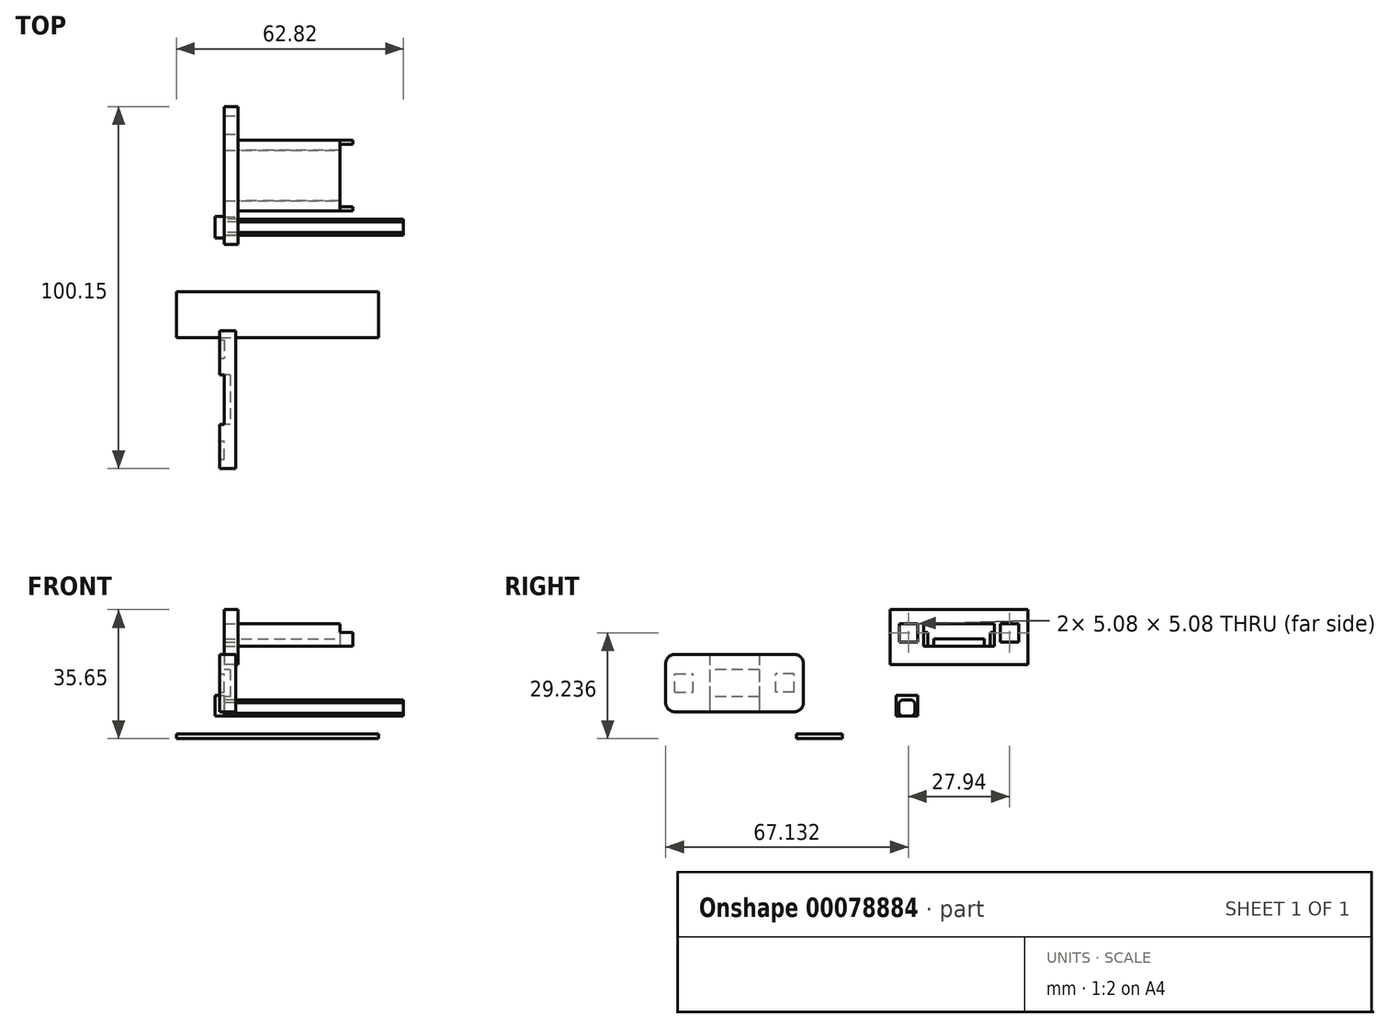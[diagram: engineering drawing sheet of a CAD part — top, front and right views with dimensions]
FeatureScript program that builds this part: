
annotation { "Feature Type Name" : "Feature", "Feature Type Description" : "" }
export const myFeature = defineFeature(function(context is Context, id is Id, definition is map)
    precondition{}
    {
        {
            var Q0;
            Q0=qCreatedBy(makeId("Front.planeOp"),FACE);
            var sketch = newSketch(context, id + "F0", { "sketchPlane" : qUnion([Q0])});
            skLineSegment(sketch, "E0.bottom", {"start": v(-13.29, 11.9) * mm, "end": v(42.6, 11.9) * mm});
            skLineSegment(sketch, "E0.top", {"start": v(-13.29, 10.63) * mm, "end": v(42.6, 10.63) * mm});
            skLineSegment(sketch, "E0.left", {"start": v(-13.29, 11.9) * mm, "end": v(-13.29, 10.63) * mm});
            skLineSegment(sketch, "E0.right", {"start": v(42.6, 11.9) * mm, "end": v(42.6, 10.63) * mm});
            skLineSegment(sketch, "E1.bottom", {"start": v(42.6, 11.9) * mm, "end": v(29.9, 11.9) * mm});
            skLineSegment(sketch, "E1.top", {"start": v(42.6, 16.98) * mm, "end": v(29.9, 16.98) * mm});
            skLineSegment(sketch, "E1.left", {"start": v(42.6, 11.9) * mm, "end": v(42.6, 16.98) * mm});
            skLineSegment(sketch, "E1.right", {"start": v(29.9, 11.9) * mm, "end": v(29.9, 16.98) * mm});
            skSolve(sketch);
        }
        {
            var Q0;
            Q0=makeQuery(id+"F0.imprint","IMPRINT",FACE,{"disambiguationData":[TD([[makeQuery(id+"F0.imprint","IMPRINT",EDGE,{"derivedFrom":sQuery(id+"F0.wireOp",EDGE,"E1.bottom")}),-1.0]])]});
            var Q1;
            Q1=makeQuery(id+"F0.imprint","IMPRINT",FACE,{"disambiguationData":[TD([[makeQuery(id+"F0.imprint","IMPRINT",EDGE,{"derivedFrom":sQuery(id+"F0.wireOp",EDGE,"E0.bottom")}),-1.0]])]});
            extrude(context, id + "F1", {"entities" : qUnion([Q0, Q1]), "depth" : 12.7 * mm});
        }
        {
            var Q0;
            Q0=qCreatedBy(makeId("Right.planeOp"),FACE);
            var sketch = newSketch(context, id + "F2", { "sketchPlane" : qUnion([Q0])});
            skLineSegment(sketch, "E2.bottom", {"start": v(-46.4, 33.9) * mm, "end": v(-13.37, 33.9) * mm});
            skLineSegment(sketch, "E2.top", {"start": v(-46.4, 18.02) * mm, "end": v(-13.37, 18.02) * mm});
            skLineSegment(sketch, "E2.left", {"start": v(-48.93, 31.35) * mm, "end": v(-48.93, 20.56) * mm});
            skLineSegment(sketch, "E2.right", {"start": v(-10.83, 31.35) * mm, "end": v(-10.83, 20.56) * mm});
            skPoint(sketch, "E3.visualSharp", {"position": v(-10.83, 33.9) * mm});
            skArc(sketch, "E3.filletArc", {"start": v(-10.83, 31.35) * mm, "mid": v(-11.58, 33.15) * mm, "end": v(-13.37, 33.9) * mm});
            skPoint(sketch, "E4.visualSharp", {"position": v(-48.93, 33.9) * mm});
            skArc(sketch, "E4.filletArc", {"start": v(-46.4, 33.9) * mm, "mid": v(-48.19, 33.15) * mm, "end": v(-48.93, 31.35) * mm});
            skPoint(sketch, "E5.visualSharp", {"position": v(-48.93, 18.02) * mm});
            skArc(sketch, "E5.filletArc", {"start": v(-48.93, 20.56) * mm, "mid": v(-48.19, 18.76) * mm, "end": v(-46.4, 18.02) * mm});
            skPoint(sketch, "E6.visualSharp", {"position": v(-10.83, 18.02) * mm});
            skArc(sketch, "E6.filletArc", {"start": v(-13.37, 18.02) * mm, "mid": v(-11.58, 18.76) * mm, "end": v(-10.83, 20.56) * mm});
            skSolve(sketch);
        }
        {
            var Q0;
            Q0=makeQuery(id+"F2.imprint","IMPRINT",FACE,{"disambiguationData":[TD([[makeQuery(id+"F2.imprint","IMPRINT",EDGE,{"derivedFrom":sQuery(id+"F2.wireOp",EDGE,"E2.bottom")}),-1.0]])]});
            extrude(context, id + "F3", {"entities" : qUnion([Q0]), "depth" : 3.17 * mm});
        }
        {
            var Q0;
            Q0=makeQuery(id+"F3.opExtrude","CAP_FACE",FACE,{"disambiguationData":[OSD([sQuery(id+"F2.wireOp",EDGE,"E2.bottom"),sQuery(id+"F2.wireOp",EDGE,"E2.top"),sQuery(id+"F2.wireOp",EDGE,"E2.left"),sQuery(id+"F2.wireOp",EDGE,"E2.right")])],"isStart":true});
            var sketch = newSketch(context, id + "F4", { "sketchPlane" : qUnion([Q0])});
            skLineSegment(sketch, "E7.bottom", {"start": v(23.02, 29.7) * mm, "end": v(36.74, 29.7) * mm});
            skLineSegment(sketch, "E7.top", {"start": v(23.02, 22.2) * mm, "end": v(36.74, 22.2) * mm});
            skLineSegment(sketch, "E7.left", {"start": v(23.02, 29.7) * mm, "end": v(23.02, 22.2) * mm});
            skLineSegment(sketch, "E7.right", {"start": v(36.74, 29.7) * mm, "end": v(36.74, 22.2) * mm});
            skLineSegment(sketch, "E8", {"start": v(36.74, 29.7) * mm, "end": v(36.74, 33.9) * mm});
            skLineSegment(sketch, "E9", {"start": v(36.74, 22.2) * mm, "end": v(36.74, 18.02) * mm});
            skLineSegment(sketch, "E10", {"start": v(23.02, 22.2) * mm, "end": v(10.83, 22.2) * mm});
            skLineSegment(sketch, "E11", {"start": v(36.74, 22.2) * mm, "end": v(48.93, 22.2) * mm});
            skPoint(sketch, "E12", {"position": v(29.88, 33.9) * mm});
            skPoint(sketch, "E13", {"position": v(29.88, 18.02) * mm});
            skLineSegment(sketch, "E14", {"start": v(29.88, 33.9) * mm, "end": v(29.88, 18.02) * mm});
            skPoint(sketch, "E15", {"position": v(10.83, 25.96) * mm});
            skLineSegment(sketch, "E16.MirrorCS", {"start": v(23.02, 29.7) * mm, "end": v(23.02, 33.9) * mm});
            skLineSegment(sketch, "E17", {"start": v(23.02, 22.2) * mm, "end": v(23.02, 18.02) * mm});
            skLineSegment(sketch, "E18.bottom", {"start": v(46.4, 23.42) * mm, "end": v(41.31, 23.42) * mm});
            skLineSegment(sketch, "E18.top", {"start": v(46.4, 28.5) * mm, "end": v(41.31, 28.5) * mm});
            skLineSegment(sketch, "E18.left", {"start": v(46.4, 23.42) * mm, "end": v(46.4, 28.5) * mm});
            skLineSegment(sketch, "E18.right", {"start": v(41.31, 23.42) * mm, "end": v(41.31, 28.5) * mm});
            skPoint(sketch, "E19", {"position": v(48.93, 25.96) * mm});
            skPoint(sketch, "E20", {"position": v(46.4, 25.96) * mm});
            skPoint(sketch, "E21.MirrorP", {"position": v(13.37, 25.96) * mm});
            skLineSegment(sketch, "E22.MirrorCS", {"start": v(13.37, 28.5) * mm, "end": v(18.45, 28.5) * mm});
            skPoint(sketch, "E23.MirrorP", {"position": v(18.33, 23.42) * mm});
            skLineSegment(sketch, "E24.MirrorCS", {"start": v(13.37, 23.42) * mm, "end": v(13.37, 28.5) * mm});
            skLineSegment(sketch, "E25.MirrorCS", {"start": v(13.37, 23.42) * mm, "end": v(18.45, 23.42) * mm});
            skLineSegment(sketch, "E26.MirrorCS", {"start": v(18.45, 23.42) * mm, "end": v(18.45, 28.5) * mm});
            skLineSegment(sketch, "E27", {"start": v(46.4, 23.42) * mm, "end": v(48.93, 23.42) * mm});
            skSolve(sketch);
        }
        {
            var Q0;
            {var subQ0=sQuery(id+"F4.wireOp",EDGE,"E7.left");Q0=makeQuery(id+"F4.imprint","IMPRINT",FACE,{"disambiguationData":[TD([[makeQuery(id+"F4.imprint","IMPRINT",EDGE,{"derivedFrom":subQ0}),1.0]])]});}
            var Q1;
            {var subQ0=sQuery(id+"F4.wireOp",EDGE,"E7.right");Q1=makeQuery(id+"F4.imprint","IMPRINT",FACE,{"disambiguationData":[TD([[makeQuery(id+"F4.imprint","IMPRINT",EDGE,{"derivedFrom":subQ0}),-1.0]])]});}
            extrude(context, id + "F5", {"entities" : qUnion([Q0, Q1]), "operationType" : NewBodyOperationType.REMOVE, "oppositeDirection" : true, "depth" : 1.59 * mm});
        }
        {
            var Q0;
            {var subQ7=sQuery(id+"F4.wireOp",EDGE,"E7.left");Q0=makeQuery(id+"F4.imprint","IMPRINT",FACE,{"disambiguationData":[TD([[makeQuery(id+"F4.imprint","IMPRINT",EDGE,{"derivedFrom":subQ7}),-1.0]])]});}
            var Q1;
            {var subQ0=sQuery(id+"F4.wireOp",EDGE,"E10");Q1=makeQuery(id+"F4.imprint","IMPRINT",FACE,{"disambiguationData":[TD([[makeQuery(id+"F4.imprint","IMPRINT",EDGE,{"derivedFrom":subQ0}),1.0]])]});}
            var Q2;
            {var subQ0=sQuery(id+"F4.wireOp",EDGE,"E11");Q2=makeQuery(id+"F4.imprint","IMPRINT",FACE,{"disambiguationData":[TD([[makeQuery(id+"F4.imprint","IMPRINT",EDGE,{"derivedFrom":subQ0}),-1.0]])]});}
            var Q3;
            {var subQ7=sQuery(id+"F4.wireOp",EDGE,"E7.right");Q3=makeQuery(id+"F4.imprint","IMPRINT",FACE,{"disambiguationData":[TD([[makeQuery(id+"F4.imprint","IMPRINT",EDGE,{"derivedFrom":subQ7}),1.0]])]});}
            extrude(context, id + "F6", {"entities" : qUnion([Q0, Q1, Q2, Q3]), "operationType" : NewBodyOperationType.ADD, "depth" : 1.27 * mm});
        }
        {
            var Q0;
            Q0=qCreatedBy(makeId("Right.planeOp"),FACE);
            var sketch = newSketch(context, id + "F7", { "sketchPlane" : qUnion([Q0])});
            skLineSegment(sketch, "E28.bottom", {"start": v(15.62, 21.36) * mm, "end": v(19.3, 21.36) * mm});
            skLineSegment(sketch, "E28.top", {"start": v(15.62, 16.91) * mm, "end": v(20.06, 16.91) * mm});
            skLineSegment(sketch, "E28.left", {"start": v(15.62, 21.36) * mm, "end": v(15.62, 16.91) * mm});
            skLineSegment(sketch, "E28.right", {"start": v(20.06, 21.36) * mm, "end": v(20.06, 20.6) * mm});
            skLineSegment(sketch, "E29", {"start": v(19.3, 21.36) * mm, "end": v(20.06, 21.36) * mm});
            skLineSegment(sketch, "E30", {"start": v(20.06, 20.6) * mm, "end": v(20.06, 16.91) * mm});
            skLineSegment(sketch, "E31", {"start": v(20.06, 20.6) * mm, "end": v(19.3, 21.36) * mm});
            skLineSegment(sketch, "E32", {"start": v(17.84, 16.91) * mm, "end": v(17.84, 18.3) * mm});
            skLineSegment(sketch, "E33", {"start": v(15.62, 19.14) * mm, "end": v(16.82, 19.14) * mm});
            skPoint(sketch, "E33.endSnap0", {"position": v(15.62, 19.14) * mm});
            skLineSegment(sketch, "E34.MirrorCS", {"start": v(15.62, 20.6) * mm, "end": v(16.38, 21.36) * mm});
            skLineSegment(sketch, "E35.MirrorCS", {"start": v(15.62, 17.68) * mm, "end": v(16.38, 16.91) * mm});
            skLineSegment(sketch, "E36.MirrorCS", {"start": v(20.06, 17.68) * mm, "end": v(19.3, 16.91) * mm});
            skLineSegment(sketch, "E37", {"start": v(20.06, 16.91) * mm, "end": v(20.82, 16.91) * mm});
            skLineSegment(sketch, "E38", {"start": v(20.82, 16.91) * mm, "end": v(20.82, 22.63) * mm});
            skLineSegment(sketch, "E39", {"start": v(20.82, 22.63) * mm, "end": v(14.85, 22.63) * mm});
            skLineSegment(sketch, "E40", {"start": v(14.85, 22.63) * mm, "end": v(14.85, 16.91) * mm});
            skLineSegment(sketch, "E41", {"start": v(14.85, 16.91) * mm, "end": v(15.62, 16.91) * mm});
            skLineSegment(sketch, "E42", {"start": v(20.06, 21.36) * mm, "end": v(20.06, 22.63) * mm});
            skSolve(sketch);
        }
        {
            var Q0;
            {var subQ3=sQuery(id+"F7.wireOp",EDGE,"E31");Q0=makeQuery(id+"F7.imprint","IMPRINT",FACE,{"disambiguationData":[TD([[makeQuery(id+"F7.imprint","IMPRINT",EDGE,{"derivedFrom":subQ3}),1.0]])]});}
            extrude(context, id + "F8", {"entities" : qUnion([Q0]), "depth" : 49.53 * mm});
        }
        {
            var Q0;
            {var subQ3=sQuery(id+"F7.wireOp",EDGE,"E28.right");Q0=makeQuery(id+"F7.imprint","IMPRINT",FACE,{"disambiguationData":[TD([[makeQuery(id+"F7.imprint","IMPRINT",EDGE,{"derivedFrom":subQ3}),1.0]])]});}
            var Q1;
            {var subQ3=sQuery(id+"F7.wireOp",EDGE,"E31");Q1=makeQuery(id+"F7.imprint","IMPRINT",FACE,{"disambiguationData":[TD([[makeQuery(id+"F7.imprint","IMPRINT",EDGE,{"derivedFrom":subQ3}),1.0]])]});}
            var Q2;
            {var subQ3=sQuery(id+"F7.wireOp",EDGE,"E36.MirrorCS");Q2=makeQuery(id+"F7.imprint","IMPRINT",FACE,{"disambiguationData":[TD([[makeQuery(id+"F7.imprint","IMPRINT",EDGE,{"derivedFrom":subQ3}),1.0]])]});}
            var Q3;
            {var subQ3=sQuery(id+"F7.wireOp",EDGE,"E35.MirrorCS");Q3=makeQuery(id+"F7.imprint","IMPRINT",FACE,{"disambiguationData":[TD([[makeQuery(id+"F7.imprint","IMPRINT",EDGE,{"derivedFrom":subQ3}),-1.0]])]});}
            var Q4;
            {var subQ3=sQuery(id+"F7.wireOp",EDGE,"E34.MirrorCS");Q4=makeQuery(id+"F7.imprint","IMPRINT",FACE,{"disambiguationData":[TD([[makeQuery(id+"F7.imprint","IMPRINT",EDGE,{"derivedFrom":subQ3}),1.0]])]});}
            var Q5;
            Q5=makeQuery(id+"F7.imprint","IMPRINT",FACE,{"disambiguationData":[TD([[makeQuery(id+"F7.imprint","IMPRINT",EDGE,{"derivedFrom":sQuery(id+"F7.wireOp",EDGE,"E28.right")}),-1.0]])]});
            var Q6;
            {var subQ1=sQuery(id+"F7.wireOp",EDGE,"E29");Q6=makeQuery(id+"F7.imprint","IMPRINT",FACE,{"disambiguationData":[TD([[makeQuery(id+"F7.imprint","IMPRINT",EDGE,{"derivedFrom":subQ1}),1.0]])]});}
            extrude(context, id + "F9", {"entities" : qUnion([Q0, Q1, Q2, Q3, Q4, Q5, Q6]), "operationType" : NewBodyOperationType.ADD, "oppositeDirection" : true, "depth" : 2.54 * mm});
        }
        {
            var Q0;
            Q0=qCreatedBy(makeId("Right.planeOp"),FACE);
            var sketch = newSketch(context, id + "F10", { "sketchPlane" : qUnion([Q0])});
            skLineSegment(sketch, "E43.bottom", {"start": v(13.12, 46.28) * mm, "end": v(51.22, 46.28) * mm});
            skLineSegment(sketch, "E43.top", {"start": v(13.12, 31.04) * mm, "end": v(51.22, 31.04) * mm});
            skLineSegment(sketch, "E43.left", {"start": v(13.12, 46.28) * mm, "end": v(13.12, 31.04) * mm});
            skLineSegment(sketch, "E43.right", {"start": v(51.22, 46.28) * mm, "end": v(51.22, 31.04) * mm});
            skSolve(sketch);
        }
        {
            var Q0;
            Q0=makeQuery(id+"F10.imprint","IMPRINT",FACE,{"disambiguationData":[TD([[makeQuery(id+"F10.imprint","IMPRINT",EDGE,{"derivedFrom":sQuery(id+"F10.wireOp",EDGE,"E43.bottom")}),-1.0]])]});
            extrude(context, id + "F11", {"entities" : qUnion([Q0]), "depth" : 3.8 * mm});
        }
        {
            var Q0;
            Q0=makeQuery(id+"F11.opExtrude","CAP_FACE",FACE,{"disambiguationData":[OSD([sQuery(id+"F10.wireOp",EDGE,"E43.bottom"),sQuery(id+"F10.wireOp",EDGE,"E43.top"),sQuery(id+"F10.wireOp",EDGE,"E43.left"),sQuery(id+"F10.wireOp",EDGE,"E43.right")])],"isStart":false});
            var sketch = newSketch(context, id + "F12", { "sketchPlane" : qUnion([Q0])});
            skPoint(sketch, "E44", {"position": v(32.17, 46.28) * mm});
            skLineSegment(sketch, "E45.bottom", {"start": v(25.19, 38.15) * mm, "end": v(39.16, 38.15) * mm});
            skLineSegment(sketch, "E45.top", {"start": v(25.19, 36.12) * mm, "end": v(39.16, 36.12) * mm});
            skLineSegment(sketch, "E45.left", {"start": v(25.19, 38.15) * mm, "end": v(25.19, 36.12) * mm});
            skLineSegment(sketch, "E45.right", {"start": v(39.16, 38.15) * mm, "end": v(39.16, 36.12) * mm});
            skPoint(sketch, "E46", {"position": v(32.17, 38.15) * mm});
            skPoint(sketch, "E47", {"position": v(25.19, 37.14) * mm});
            skLineSegment(sketch, "E48", {"start": v(32.17, 38.15) * mm, "end": v(32.17, 46.28) * mm});
            skLineSegment(sketch, "E49.bottom", {"start": v(20.74, 37.33) * mm, "end": v(15.66, 37.33) * mm});
            skLineSegment(sketch, "E49.top", {"start": v(20.74, 42.4) * mm, "end": v(15.66, 42.4) * mm});
            skLineSegment(sketch, "E49.left", {"start": v(20.74, 37.33) * mm, "end": v(20.74, 42.4) * mm});
            skLineSegment(sketch, "E49.right", {"start": v(15.66, 37.33) * mm, "end": v(15.66, 42.4) * mm});
            skPoint(sketch, "E50", {"position": v(20.74, 39.87) * mm});
            skLineSegment(sketch, "E51", {"start": v(15.66, 37.33) * mm, "end": v(13.12, 37.33) * mm});
            skLineSegment(sketch, "E52.MirrorCS", {"start": v(43.6, 42.4) * mm, "end": v(48.68, 42.4) * mm});
            skLineSegment(sketch, "E53.MirrorCS", {"start": v(43.6, 37.33) * mm, "end": v(48.68, 37.33) * mm});
            skLineSegment(sketch, "E54.MirrorCS", {"start": v(43.6, 37.33) * mm, "end": v(43.6, 42.4) * mm});
            skLineSegment(sketch, "E55.MirrorCS", {"start": v(48.68, 37.33) * mm, "end": v(48.68, 42.4) * mm});
            skPoint(sketch, "E56.MirrorP", {"position": v(43.6, 39.87) * mm});
            skLineSegment(sketch, "E57", {"start": v(32.17, 36.12) * mm, "end": v(32.17, 31.04) * mm});
            skLineSegment(sketch, "E58", {"start": v(43.6, 42.4) * mm, "end": v(43.6, 46.28) * mm});
            skLineSegment(sketch, "E59", {"start": v(25.19, 36.12) * mm, "end": v(22.4, 36.12) * mm});
            skLineSegment(sketch, "E60", {"start": v(39.16, 36.12) * mm, "end": v(41.95, 36.12) * mm});
            skLineSegment(sketch, "E61", {"start": v(22.4, 36.12) * mm, "end": v(13.12, 36.12) * mm});
            skLineSegment(sketch, "E62", {"start": v(41.95, 36.12) * mm, "end": v(51.22, 36.12) * mm});
            skLineSegment(sketch, "E63", {"start": v(22.4, 36.12) * mm, "end": v(22.4, 42.42) * mm});
            skLineSegment(sketch, "E64", {"start": v(22.4, 42.42) * mm, "end": v(41.95, 42.42) * mm});
            skLineSegment(sketch, "E65", {"start": v(41.95, 42.42) * mm, "end": v(41.95, 36.12) * mm});
            skLineSegment(sketch, "E66.bottom", {"start": v(13.12, 46.28) * mm, "end": v(51.22, 46.28) * mm});
            skLineSegment(sketch, "E66.top", {"start": v(13.12, 31.04) * mm, "end": v(51.22, 31.04) * mm});
            skLineSegment(sketch, "E66.left", {"start": v(13.12, 46.28) * mm, "end": v(13.12, 31.04) * mm});
            skLineSegment(sketch, "E66.right", {"start": v(51.22, 46.28) * mm, "end": v(51.22, 31.04) * mm});
            skSolve(sketch);
        }
        {
            var Q0;
            {var subQ4=sQuery(id+"F12.wireOp",EDGE,"E45.top");Q0=makeQuery(id+"F12.imprint","IMPRINT",FACE,{"disambiguationData":[TD([[makeQuery(id+"F12.imprint","IMPRINT",EDGE,{"derivedFrom":subQ4}),1.0]])]});}
            var Q1;
            Q1=makeQuery(id+"F12.imprint","IMPRINT",FACE,{"disambiguationData":[TD([[makeQuery(id+"F12.imprint","IMPRINT",EDGE,{"derivedFrom":sQuery(id+"F12.wireOp",EDGE,"E52.MirrorCS")}),-1.0]])]});
            var Q2;
            Q2=makeQuery(id+"F12.imprint","IMPRINT",FACE,{"disambiguationData":[TD([[makeQuery(id+"F12.imprint","IMPRINT",EDGE,{"derivedFrom":sQuery(id+"F12.wireOp",EDGE,"E49.bottom")}),-1.0]])]});
            extrude(context, id + "F13", {"entities" : qUnion([Q0, Q1, Q2]), "operationType" : NewBodyOperationType.REMOVE, "oppositeDirection" : true, "depth" : 10.16 * mm});
        }
        {
            var Q0;
            {var subQ5=sQuery(id+"F12.wireOp",EDGE,"E45.left");Q0=makeQuery(id+"F12.imprint","IMPRINT",FACE,{"disambiguationData":[TD([[makeQuery(id+"F12.imprint","IMPRINT",EDGE,{"derivedFrom":subQ5}),-1.0]])]});}
            var Q1;
            {var subQ5=sQuery(id+"F12.wireOp",EDGE,"E45.right");Q1=makeQuery(id+"F12.imprint","IMPRINT",FACE,{"disambiguationData":[TD([[makeQuery(id+"F12.imprint","IMPRINT",EDGE,{"derivedFrom":subQ5}),1.0]])]});}
            extrude(context, id + "F14", {"entities" : qUnion([Q0, Q1]), "operationType" : NewBodyOperationType.ADD, "depth" : 31.75 * mm});
        }
        {
            var Q0;
            Q0=makeQuery(id+"F14.opExtrude","CAP_FACE",FACE,{"disambiguationData":[OSD([sQuery(id+"F12.wireOp",EDGE,"E45.bottom"),sQuery(id+"F12.wireOp",EDGE,"E45.left"),sQuery(id+"F12.wireOp",EDGE,"E45.right"),sQuery(id+"F12.wireOp",EDGE,"E59"),sQuery(id+"F12.wireOp",EDGE,"E60"),sQuery(id+"F12.wireOp",EDGE,"E63"),sQuery(id+"F12.wireOp",EDGE,"E64"),sQuery(id+"F12.wireOp",EDGE,"E65")])],"isStart":false});
            var sketch = newSketch(context, id + "F15", { "sketchPlane" : qUnion([Q0])});
            skLineSegment(sketch, "E67.bottom", {"start": v(23.54, 42.42) * mm, "end": v(40.8, 42.42) * mm});
            skLineSegment(sketch, "E67.left", {"start": v(23.54, 42.42) * mm, "end": v(23.54, 36.12) * mm});
            skLineSegment(sketch, "E67.right", {"start": v(40.8, 42.42) * mm, "end": v(40.8, 36.12) * mm});
            skLineSegment(sketch, "E68", {"start": v(22.4, 36.12) * mm, "end": v(41.95, 36.12) * mm});
            skPoint(sketch, "E69", {"position": v(32.17, 42.42) * mm});
            skPoint(sketch, "E70", {"position": v(32.17, 36.12) * mm});
            skLineSegment(sketch, "E71", {"start": v(23.54, 40.02) * mm, "end": v(22.4, 40.02) * mm});
            skLineSegment(sketch, "E72", {"start": v(32.17, 42.42) * mm, "end": v(32.17, 40.48) * mm});
            skLineSegment(sketch, "E73.MirrorCS", {"start": v(40.8, 40.02) * mm, "end": v(41.95, 40.02) * mm});
            skSolve(sketch);
        }
        {
            var Q0;
            Q0=makeQuery(id+"F15.imprint","IMPRINT",FACE,{"disambiguationData":[TD([[makeQuery(id+"F15.imprint","IMPRINT",EDGE,{"derivedFrom":makeQuery(id+"F14.opExtrude","CAP_EDGE",EDGE,{"disambiguationData":[OSD([sQuery(id+"F12.wireOp",EDGE,"E45.bottom")])],"isStart":false})}),1.0]])]});
            var Q1;
            {var subQ3=sQuery(id+"F15.wireOp",EDGE,"E71");Q1=makeQuery(id+"F15.imprint","IMPRINT",FACE,{"disambiguationData":[TD([[makeQuery(id+"F15.imprint","IMPRINT",EDGE,{"derivedFrom":subQ3}),-1.0]])]});}
            var Q2;
            {var subQ3=sQuery(id+"F15.wireOp",EDGE,"E73.MirrorCS");Q2=makeQuery(id+"F15.imprint","IMPRINT",FACE,{"disambiguationData":[TD([[makeQuery(id+"F15.imprint","IMPRINT",EDGE,{"derivedFrom":subQ3}),1.0]])]});}
            extrude(context, id + "F16", {"entities" : qUnion([Q0, Q1, Q2]), "operationType" : NewBodyOperationType.REMOVE, "oppositeDirection" : true, "depth" : 3.56 * mm});
        }
    });
